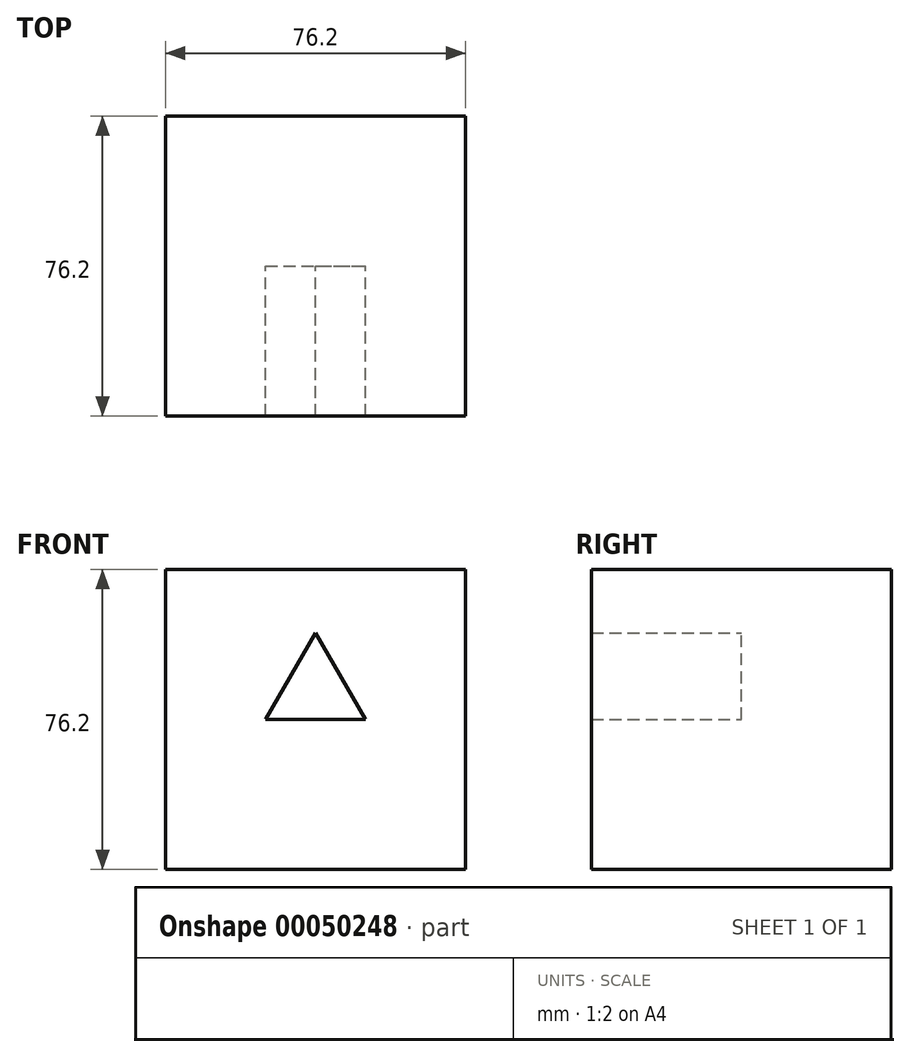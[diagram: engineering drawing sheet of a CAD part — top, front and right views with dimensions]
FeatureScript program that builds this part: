
annotation { "Feature Type Name" : "Feature", "Feature Type Description" : "" }
export const myFeature = defineFeature(function(context is Context, id is Id, definition is map)
    precondition{}
    {
        {
            var Q0;
            Q0=qCreatedBy(makeId("Front.planeOp"),FACE);
            var sketch = newSketch(context, id + "F0", { "sketchPlane" : qUnion([Q0])});
            skLineSegment(sketch, "E0.rect.bottom", {"start": v(38.1, 38.1) * mm, "end": v(-38.1, 38.1) * mm});
            skLineSegment(sketch, "E0.rect.top", {"start": v(38.1, -38.1) * mm, "end": v(-38.1, -38.1) * mm});
            skLineSegment(sketch, "E0.rect.left", {"start": v(38.1, 38.1) * mm, "end": v(38.1, -38.1) * mm});
            skLineSegment(sketch, "E0.rect.right", {"start": v(-38.1, 38.1) * mm, "end": v(-38.1, -38.1) * mm});
            skPoint(sketch, "E0.rect.middle", {"position": v(0, 0) * mm});
            skSolve(sketch);
        }
        {
            var Q0;
            Q0=makeQuery(id+"F0.imprint","IMPRINT",FACE,{"disambiguationData":[TD([[makeQuery(id+"F0.imprint","IMPRINT",EDGE,{"derivedFrom":sQuery(id+"F0.wireOp",EDGE,"E0.rect.bottom")}),1.0]])]});
            extrude(context, id + "F1", {"entities" : qUnion([Q0]), "endBound" : BoundingType.SYMMETRIC, "depth" : 76.2 * mm});
        }
        {
            var Q0;
            Q0=qCreatedBy(makeId("Front.planeOp"),FACE);
            var sketch = newSketch(context, id + "F2", { "sketchPlane" : qUnion([Q0])});
            skLineSegment(sketch, "E1", {"start": v(-12.7, 0) * mm, "end": v(12.7, 0) * mm});
            skLineSegment(sketch, "E2", {"start": v(-12.7, 0) * mm, "end": v(0, 22) * mm});
            skLineSegment(sketch, "E3", {"start": v(0, 22) * mm, "end": v(12.7, 0) * mm});
            skSolve(sketch);
        }
        {
            var Q0;
            Q0=makeQuery(id+"F2.imprint","IMPRINT",FACE,{"disambiguationData":[TD([[makeQuery(id+"F2.imprint","IMPRINT",EDGE,{"derivedFrom":sQuery(id+"F2.wireOp",EDGE,"E1")}),1.0]])]});
            extrude(context, id + "F3", {"entities" : qUnion([Q0]), "operationType" : NewBodyOperationType.REMOVE, "endBound" : BoundingType.THROUGH_ALL, "depth" : 76.2 * mm});
        }
    });
